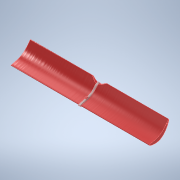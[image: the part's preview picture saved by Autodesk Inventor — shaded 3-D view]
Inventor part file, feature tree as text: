
AUTODESK INVENTOR PART (.ipt)
format: ipt  version: 2022 (Build 260153000, 153)  size: 4,598,272 bytes
history: mixed  units: in
note: dims shown in document units (in); Inventor stores cm internally (conversion verified against a paired STEP export)
features: other x18, sketch x7, extrude x6, mirror x1, fillet x1, imported_body x1
ambient origin geometry x8: Origin, YZ Plane, XZ Plane, XY Plane, X Axis, Y Axis, Z Axis, Center Point
bodies: Solido2 (imported_parasolid), Solido6 (imported_parasolid), Solido7 (imported_parasolid)
feature tree (34):
  other  "Elimina faccia1"
  other  "Elimina faccia2"
  other  "Elimina faccia3"
  other  "Elimina faccia4"
  other  "Elimina faccia5"
  other  "Elimina faccia6"
  other  "Elimina faccia7"
  other  "Elimina faccia8"
  other  "Elimina faccia9"
  other  "Piano di lavoro14"
  extrude  "Estrusione11"  Depth=16.0236in
  extrude  "Estrusione12"  Depth=0.0039in TaperAngle=0.0deg
  mirror  "Specchio2"
  other  "Elimina faccia10"
  other  "Elimina faccia11"
  other  "Elimina faccia12"
  other  "Elimina faccia13"
  other  "Elimina faccia14"
  other  "Elimina faccia15"
  other  "Piano di lavoro15"
  extrude  "Estrusione13"  Depth=0.1969in
  extrude  "Estrusione14"  Depth=0.7874in
  other  "Piano di lavoro16"
  sketch  "Schizzo24"
  sketch  "Schizzo25"
  extrude  "Estrusione15"  Depth=0.0984in TaperAngle=0.0deg
  extrude  "Estrusione16"  Depth=16.0236in
  sketch  "Schizzo20"
  sketch  "Schizzo21"
  sketch  "Schizzo22"
  sketch  "Schizzo23"
  sketch  "Schizzo27"
  fillet  "Fillet30"  Radius=0.0039in
  imported_body  NMx_Import_Brep_tag  [imported B-rep: ~9 faces, bbox_mm=None]
